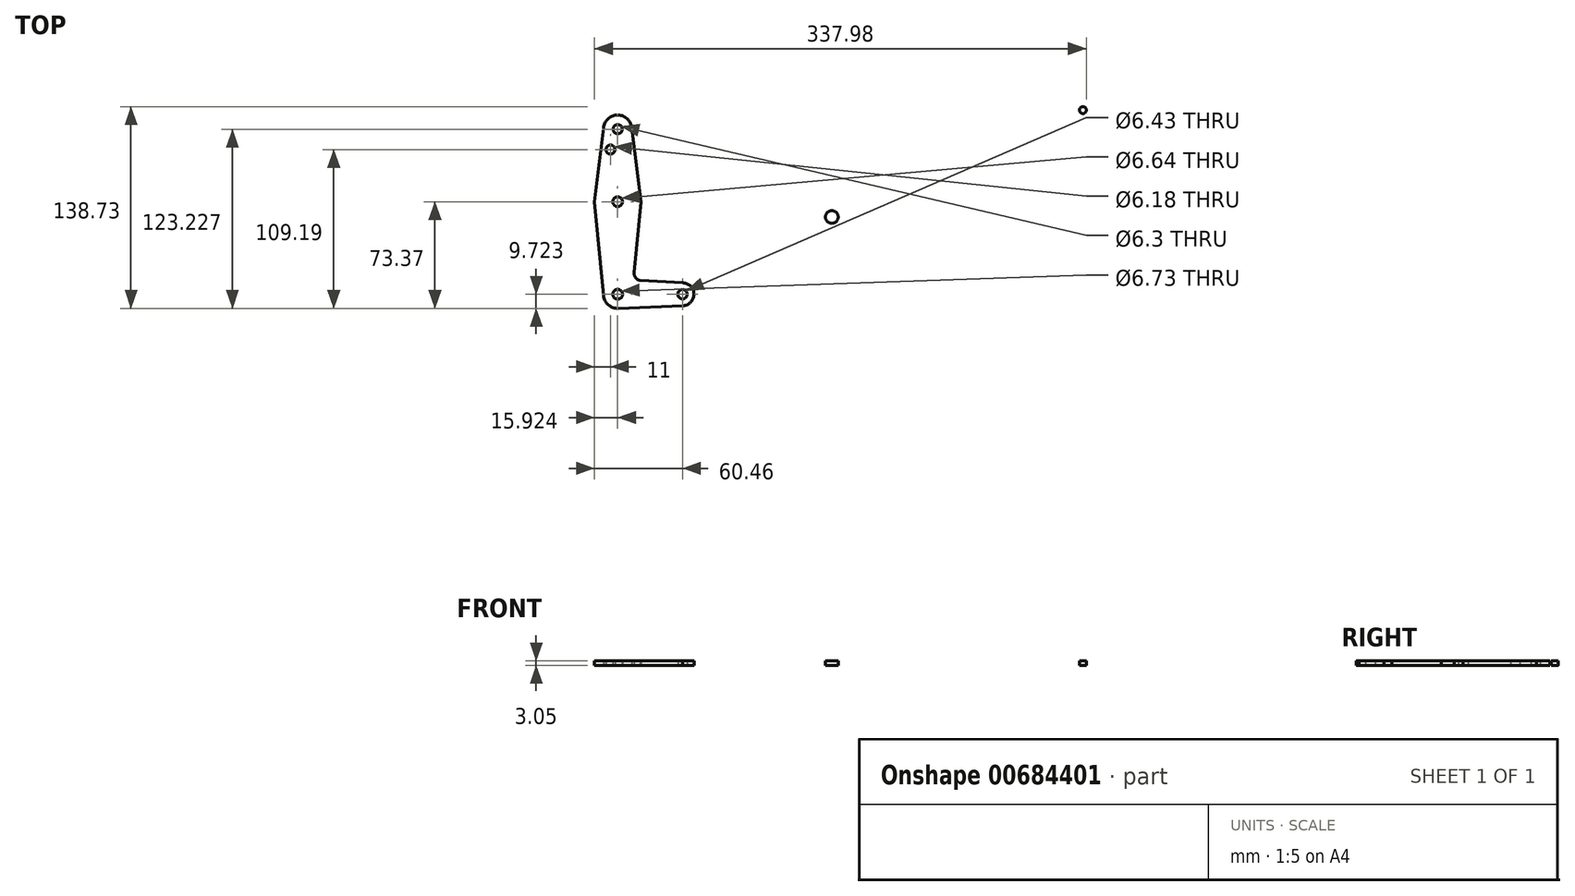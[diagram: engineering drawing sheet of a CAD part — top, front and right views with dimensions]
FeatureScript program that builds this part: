
annotation { "Feature Type Name" : "Feature", "Feature Type Description" : "" }
export const myFeature = defineFeature(function(context is Context, id is Id, definition is map)
    precondition{}
    {
        {
            var Q0;
            Q0=qCreatedBy(makeId("Top.planeOp"),FACE);
            var sketch = newSketch(context, id + "F0", { "sketchPlane" : qUnion([Q0])});
            skCircle(sketch, "E0", {"center": v(-140.28, 49.86) * mm, "radius": 9.69 * mm});
            skLineSegment(sketch, "E1", {"start": v(-140.28, 49.86) * mm, "end": v(-140.28, 0) * mm});
            skCircle(sketch, "E2", {"center": v(-140.28, 0) * mm, "radius": 15.8 * mm});
            skLineSegment(sketch, "E3", {"start": v(-140.28, 0) * mm, "end": v(-140.28, -53.93) * mm});
            skCircle(sketch, "E4", {"center": v(-140.28, -63.65) * mm, "radius": 9.72 * mm});
            skLineSegment(sketch, "E5", {"start": v(-140.28, -63.65) * mm, "end": v(-136.91, -63.65) * mm});
            skCircle(sketch, "E6", {"center": v(-95.74, -63.65) * mm, "radius": 7.87 * mm});
            skLineSegment(sketch, "E7", {"start": v(-130.6, 50.36) * mm, "end": v(-124.35, 0) * mm});
            skLineSegment(sketch, "E8", {"start": v(-124.35, 0) * mm, "end": v(-129.1, -48.8) * mm});
            skLineSegment(sketch, "E9", {"start": v(-149.86, 51.27) * mm, "end": v(-156.2, 0) * mm});
            skLineSegment(sketch, "E10", {"start": v(-156.2, 0) * mm, "end": v(-149.95, -64.58) * mm});
            skLineSegment(sketch, "E11", {"start": v(-95.33, -55.78) * mm, "end": v(-124.99, -54.22) * mm});
            skLineSegment(sketch, "E12", {"start": v(-95.28, -71.5) * mm, "end": v(-139.87, -73.36) * mm});
            skCircle(sketch, "E13", {"center": v(-140.28, 49.86) * mm, "radius": 3.15 * mm});
            skCircle(sketch, "E14", {"center": v(179.4, 62.99) * mm, "radius": 2.37 * mm});
            skCircle(sketch, "E15", {"center": v(-145.2, 35.82) * mm, "radius": 3.09 * mm});
            skCircle(sketch, "E16", {"center": v(-140.28, 0) * mm, "radius": 3.32 * mm});
            skCircle(sketch, "E17", {"center": v(-140.28, -63.65) * mm, "radius": 3.37 * mm});
            skCircle(sketch, "E18", {"center": v(-95.74, -63.65) * mm, "radius": 3.22 * mm});
            skCircle(sketch, "E19", {"center": v(6.88, -10.55) * mm, "radius": 4.37 * mm});
            skPoint(sketch, "E20.orphan", {"position": v(-140.28, -53.42) * mm});
            skArc(sketch, "E21", {"start": v(-129, -47.72) * mm, "mid": v(-127.52, -52.72) * mm, "end": v(-122.56, -54.35) * mm});
            skPoint(sketch, "E21.first.point", {"position": v(-129, -47.72) * mm});
            skPoint(sketch, "E21.second.point", {"position": v(-122.56, -54.35) * mm});
            skPoint(sketch, "E21.third.point", {"position": v(-121.07, -43.73) * mm});
            skLineSegment(sketch, "E22.trimOffspring", {"start": v(-130.56, -63.65) * mm, "end": v(-95.74, -63.65) * mm});
            skLineSegment(sketch, "E23.trimOffspring", {"start": v(-140.28, -60.28) * mm, "end": v(-140.28, -63.65) * mm});
            skSolve(sketch);
        }
        {
            var Q0;
            Q0 = qSketchRegion(id + "F0", true);
            extrude(context, id + "F1", {"entities" : qUnion([Q0]), "depth" : 3.05 * mm, "offsetDistance" : 25.4 * mm});
        }
    });
